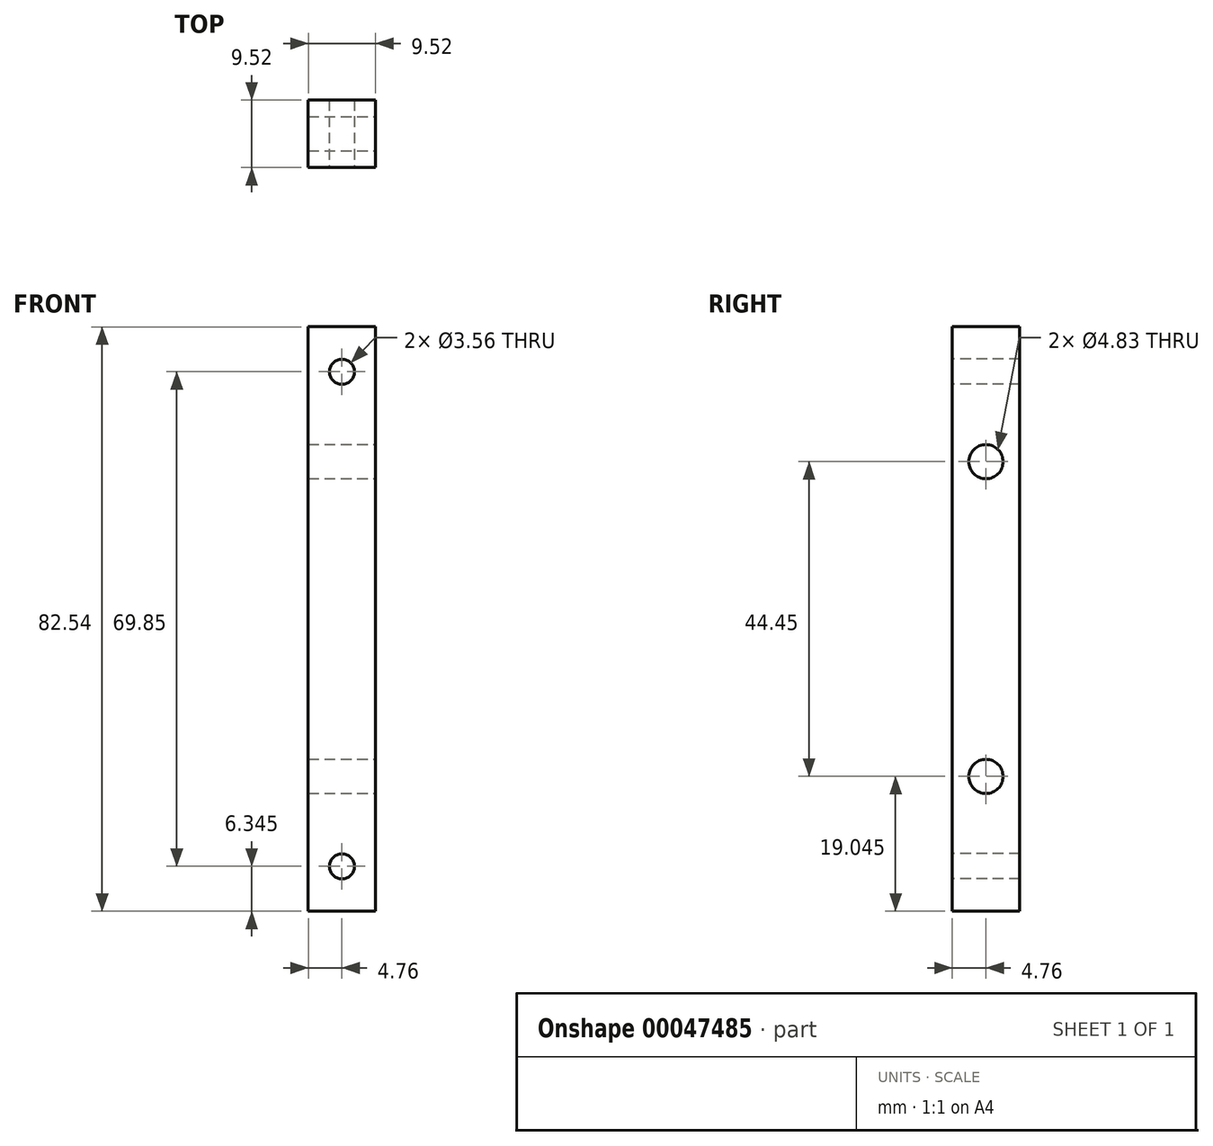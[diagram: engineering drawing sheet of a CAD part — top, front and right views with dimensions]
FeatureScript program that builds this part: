
annotation { "Feature Type Name" : "Feature", "Feature Type Description" : "" }
export const myFeature = defineFeature(function(context is Context, id is Id, definition is map)
    precondition{}
    {
        {
            var Q0;
            Q0=qCreatedBy(makeId("Top.planeOp"),FACE);
            var sketch = newSketch(context, id + "F0", { "sketchPlane" : qUnion([Q0])});
            skLineSegment(sketch, "E0.rect.bottom", {"start": v(-4.76, 4.76) * mm, "end": v(4.76, 4.76) * mm});
            skLineSegment(sketch, "E0.rect.top", {"start": v(-4.76, -4.76) * mm, "end": v(4.76, -4.76) * mm});
            skLineSegment(sketch, "E0.rect.left", {"start": v(-4.76, 4.76) * mm, "end": v(-4.76, -4.76) * mm});
            skLineSegment(sketch, "E0.rect.right", {"start": v(4.76, 4.76) * mm, "end": v(4.76, -4.76) * mm});
            skPoint(sketch, "E0.rect.middle", {"position": v(0, 0) * mm});
            skSolve(sketch);
        }
        {
            var Q0;
            Q0 = qSketchRegion(id + "F0", true);
            extrude(context, id + "F1", {"entities" : qUnion([Q0]), "depth" : 82.55 * mm, "symmetric" : true});
        }
        {
            var Q0;
            Q0=makeQuery(id+"F1.opExtrude","SWEPT_FACE",FACE,{"disambiguationData":[OSD([sQuery(id+"F0.wireOp",EDGE,"E0.rect.top")])]});
            var sketch = newSketch(context, id + "F2", { "sketchPlane" : qUnion([Q0])});
            skCircle(sketch, "E1", {"center": v(0, 34.93) * mm, "radius": 1.78 * mm});
            skCircle(sketch, "E2", {"center": v(0, -34.92) * mm, "radius": 1.78 * mm});
            skSolve(sketch);
        }
        {
            var Q0;
            Q0 = qSketchRegion(id + "F2", true);
            extrude(context, id + "F3", {"entities" : qUnion([Q0]), "operationType" : NewBodyOperationType.REMOVE, "oppositeDirection" : true, "depth" : 9.52 * mm});
        }
        {
            var Q0;
            Q0=makeQuery(id+"F1.opExtrude","SWEPT_FACE",FACE,{"disambiguationData":[OSD([sQuery(id+"F0.wireOp",EDGE,"E0.rect.right")])]});
            var sketch = newSketch(context, id + "F4", { "sketchPlane" : qUnion([Q0])});
            skCircle(sketch, "E3", {"center": v(0, 22.23) * mm, "radius": 2.41 * mm});
            skCircle(sketch, "E4", {"center": v(0, -22.22) * mm, "radius": 2.41 * mm});
            skSolve(sketch);
        }
        {
            var Q0;
            Q0 = qSketchRegion(id + "F4", true);
            extrude(context, id + "F5", {"entities" : qUnion([Q0]), "operationType" : NewBodyOperationType.REMOVE, "oppositeDirection" : true, "depth" : 9.52 * mm});
        }
    });
